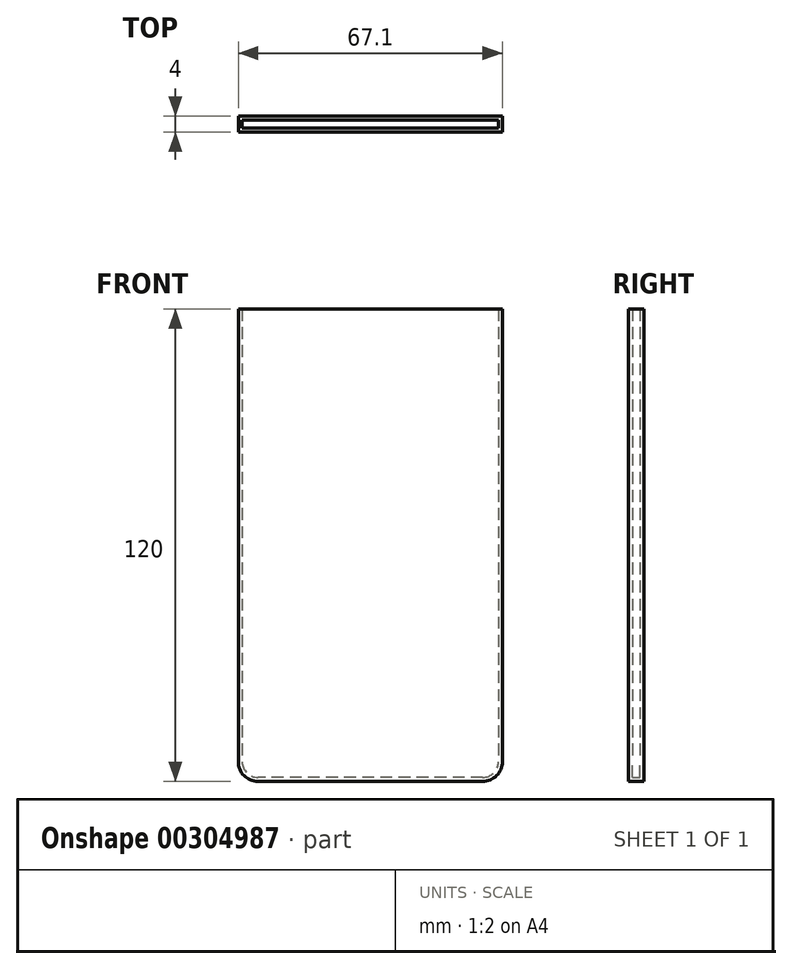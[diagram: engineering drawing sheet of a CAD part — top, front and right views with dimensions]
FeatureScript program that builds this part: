
annotation { "Feature Type Name" : "Feature", "Feature Type Description" : "" }
export const myFeature = defineFeature(function(context is Context, id is Id, definition is map)
    precondition{}
    {
        {
            var Q0;
            Q0=qCreatedBy(makeId("Front.planeOp"),FACE);
            var sketch = newSketch(context, id + "F0", { "sketchPlane" : qUnion([Q0])});
            skLineSegment(sketch, "E0.bottom", {"start": v(33.55, 60) * mm, "end": v(-33.55, 60) * mm});
            skLineSegment(sketch, "E0.top", {"start": v(33.55, -60) * mm, "end": v(-33.55, -60) * mm});
            skLineSegment(sketch, "E0.left", {"start": v(33.55, 60) * mm, "end": v(33.55, -60) * mm});
            skLineSegment(sketch, "E0.right", {"start": v(-33.55, 60) * mm, "end": v(-33.55, -60) * mm});
            skPoint(sketch, "E0.middle", {"position": v(0, 0) * mm});
            skSolve(sketch);
        }
        {
            var Q0;
            Q0=qSketchRegion(id+"F0",true);
            extrude(context, id + "F1", {"entities" : qUnion([Q0]), "depth" : 4 * mm});
        }
        {
            var Q0;
            Q0=makeQuery(id+"F1.opExtrude","SWEPT_EDGE",EDGE,{"disambiguationData":[OSD([sQuery(id+"F0.wireOp",EDGE,"E0.top"),sQuery(id+"F0.wireOp",EDGE,"E0.left")])]});
            var Q1;
            Q1=makeQuery(id+"F1.opExtrude","SWEPT_EDGE",EDGE,{"disambiguationData":[OSD([sQuery(id+"F0.wireOp",EDGE,"E0.top"),sQuery(id+"F0.wireOp",EDGE,"E0.right")])]});
            fillet(context, id + "F2", {"entities" : qUnion([Q0, Q1]), "radius" : 5 * mm, "tangentPropagation" : true, "allowEdgeOverflow" : false});
        }
        {
            var Q0;
            Q0=makeQuery(id+"F1.opExtrude","SWEPT_FACE",FACE,{"disambiguationData":[OSD([sQuery(id+"F0.wireOp",EDGE,"E0.bottom")])]});
            shell(context, id + "F3", {"entities" : qUnion([Q0]), "thickness" : 1 * mm});
        }
    });
